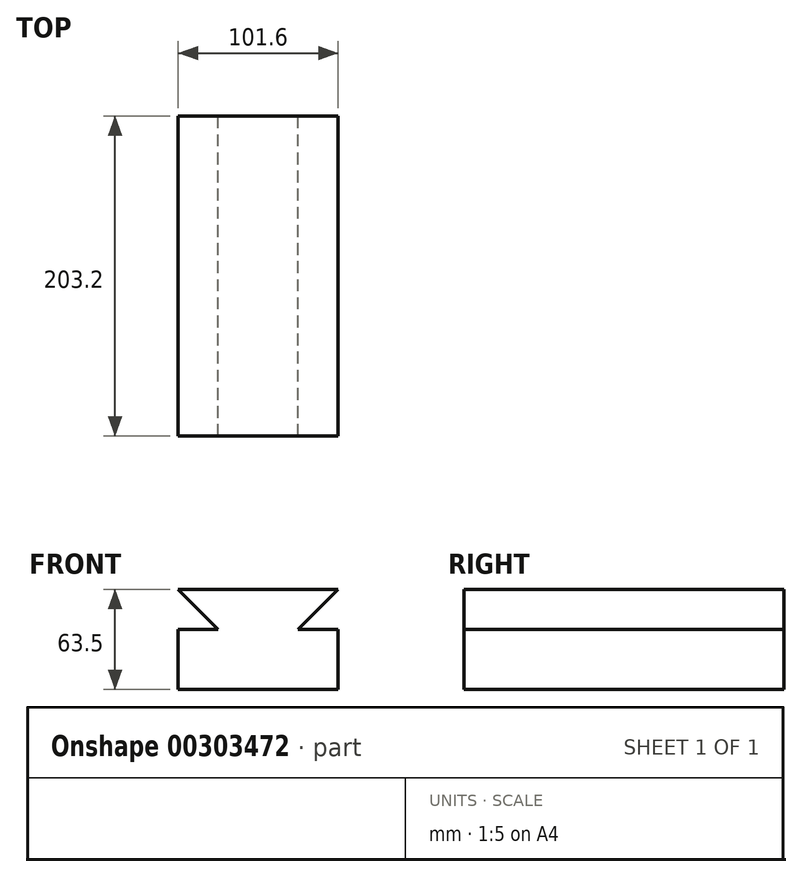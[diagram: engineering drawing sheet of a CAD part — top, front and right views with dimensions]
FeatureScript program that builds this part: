
annotation { "Feature Type Name" : "Feature", "Feature Type Description" : "" }
export const myFeature = defineFeature(function(context is Context, id is Id, definition is map)
    precondition{}
    {
        {
            var Q0;
            Q0=qCreatedBy(makeId("Front.planeOp"),FACE);
            var sketch = newSketch(context, id + "F0", { "sketchPlane" : qUnion([Q0])});
            skLineSegment(sketch, "E0.bottom", {"start": v(-66.43, 63.5) * mm, "end": v(35.17, 63.5) * mm});
            skLineSegment(sketch, "E0.top", {"start": v(-66.43, 0) * mm, "end": v(35.17, 0) * mm});
            skLineSegment(sketch, "E0.left", {"start": v(-66.43, 63.5) * mm, "end": v(-66.43, 0) * mm});
            skLineSegment(sketch, "E0.right", {"start": v(35.17, 63.5) * mm, "end": v(35.17, 0) * mm});
            skLineSegment(sketch, "E1", {"start": v(35.17, 63.5) * mm, "end": v(9.77, 38.1) * mm});
            skLineSegment(sketch, "E2", {"start": v(9.77, 38.1) * mm, "end": v(35.17, 38.1) * mm});
            skLineSegment(sketch, "E3", {"start": v(-66.43, 63.5) * mm, "end": v(-41.03, 38.1) * mm});
            skLineSegment(sketch, "E4", {"start": v(-41.03, 38.1) * mm, "end": v(-66.43, 38.1) * mm});
            skSolve(sketch);
        }
        {
            var Q0;
            Q0=makeQuery(id+"F0.imprint","IMPRINT",FACE,{"disambiguationData":[TD([[makeQuery(id+"F0.imprint","IMPRINT",EDGE,{"derivedFrom":sQuery(id+"F0.wireOp",EDGE,"E0.bottom")}),-1.0]])]});
            extrude(context, id + "F1", {"entities" : qUnion([Q0]), "depth" : 203.2 * mm});
        }
    });
